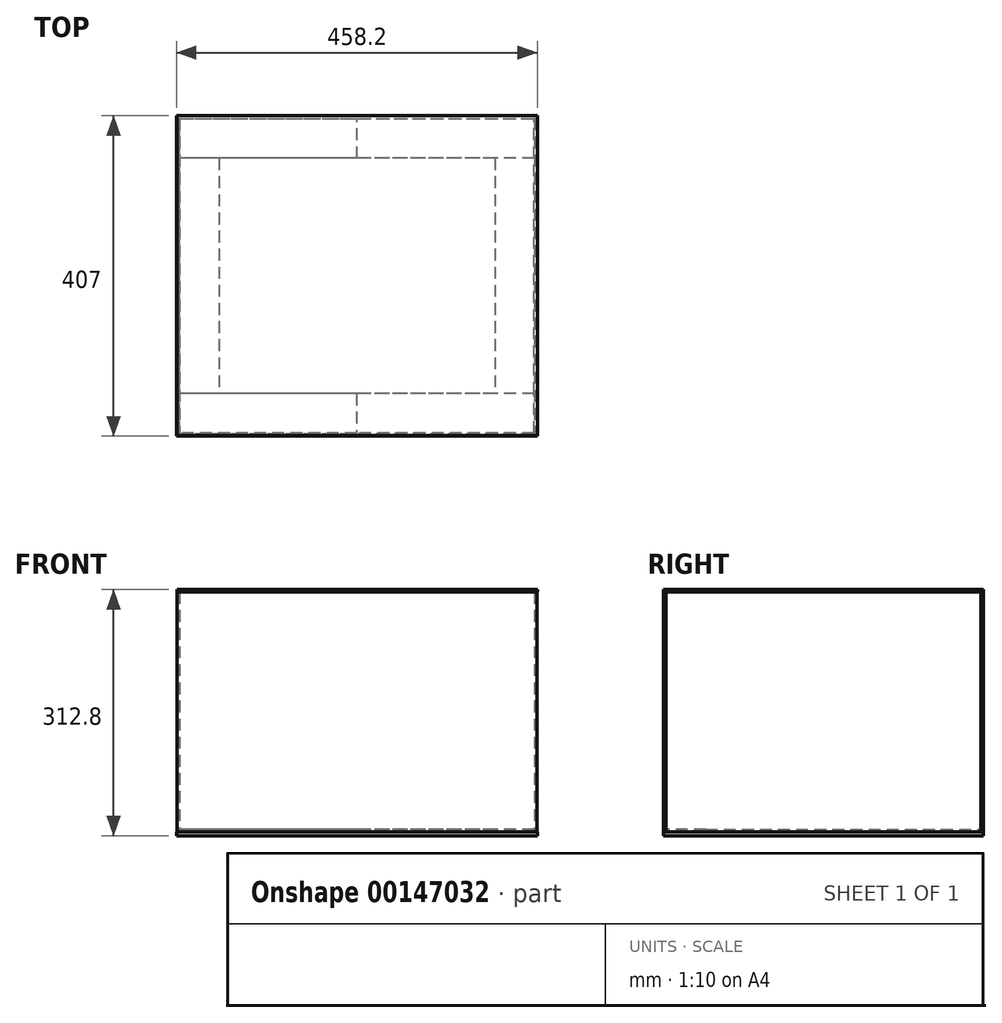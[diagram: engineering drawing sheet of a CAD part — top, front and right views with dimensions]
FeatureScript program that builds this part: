
annotation { "Feature Type Name" : "Feature", "Feature Type Description" : "" }
export const myFeature = defineFeature(function(context is Context, id is Id, definition is map)
    precondition{}
    {
        {
            assignVariable(context, id + "F0", {"name" : "perspex_sheet_width", "anyValue" : 609.6});
        }
        {
            assignVariable(context, id + "F1", {"name" : "perspex_t", "anyValue" : 3});
        }
        {
            assignVariable(context, id + "F2", {"name" : "case_z", "anyValue" : (getVariable(context, 'perspex_sheet_width') / 2) + getVariable(context, 'perspex_t')});
        }
        {
            var Q0;
            Q0=qCreatedBy(makeId("Top.planeOp"),FACE);
            var sketch = newSketch(context, id + "F3", { "sketchPlane" : qUnion([Q0])});
            skLineSegment(sketch, "E0.bottom", {"start": v(-457.7, -406.5) * mm, "end": v(-0.5, -406.5) * mm});
            skLineSegment(sketch, "E0.top", {"start": v(-457.7, -0.5) * mm, "end": v(-0.5, -0.5) * mm});
            skLineSegment(sketch, "E0.left", {"start": v(-457.7, -406.5) * mm, "end": v(-457.7, -0.5) * mm});
            skLineSegment(sketch, "E0.right", {"start": v(-0.5, -406.5) * mm, "end": v(-0.5, -0.5) * mm});
            skLineSegment(sketch, "E1.bottom", {"start": v(0, -407) * mm, "end": v(-458.2, -407) * mm});
            skLineSegment(sketch, "E1.top", {"start": v(0, 0) * mm, "end": v(-458.2, 0) * mm});
            skLineSegment(sketch, "E1.left", {"start": v(0, -407) * mm, "end": v(0, 0) * mm});
            skLineSegment(sketch, "E1.right", {"start": v(-458.2, -407) * mm, "end": v(-458.2, 0) * mm});
            skSolve(sketch);
        }
        {
            assignVariable(context, id + "F4", {"name" : "plywood_t", "anyValue" : 5});
        }
        {
            var Q0;
            Q0=makeQuery(id+"F3.imprint","IMPRINT",FACE,{"disambiguationData":[TD([[makeQuery(id+"F3.imprint","IMPRINT",EDGE,{"derivedFrom":sQuery(id+"F3.wireOp",EDGE,"E0.bottom")}),1.0]])]});
            var Q1;
            Q1=makeQuery(id+"F3.imprint","IMPRINT",FACE,{"disambiguationData":[TD([[makeQuery(id+"F3.imprint","IMPRINT",EDGE,{"derivedFrom":sQuery(id+"F3.wireOp",EDGE,"E0.bottom")}),-1.0]])]});
            extrude(context, id + "F5", {"entities" : qUnion([Q0, Q1]), "depth" : (getVariable(context, 'plywood_t')) * mm});
        }
        {
            var Q0;
            Q0=makeQuery(id+"F5.opExtrude","CAP_FACE",FACE,{"disambiguationData":[OSD([sQuery(id+"F3.wireOp",EDGE,"E1.bottom"),sQuery(id+"F3.wireOp",EDGE,"E1.top"),sQuery(id+"F3.wireOp",EDGE,"E1.left"),sQuery(id+"F3.wireOp",EDGE,"E1.right")])],"isStart":false});
            var sketch = newSketch(context, id + "F6", { "sketchPlane" : qUnion([Q0])});
            skLineSegment(sketch, "E2.bottom", {"start": v(-457.7, -406.5) * mm, "end": v(-0.5, -406.5) * mm});
            skLineSegment(sketch, "E2.top", {"start": v(-457.7, -0.5) * mm, "end": v(-0.5, -0.5) * mm});
            skLineSegment(sketch, "E2.left", {"start": v(-457.7, -406.5) * mm, "end": v(-457.7, -0.5) * mm});
            skLineSegment(sketch, "E2.right", {"start": v(-0.5, -406.5) * mm, "end": v(-0.5, -0.5) * mm});
            skLineSegment(sketch, "E3", {"start": v(-457.7, -403.5) * mm, "end": v(-0.5, -403.5) * mm});
            skLineSegment(sketch, "E4", {"start": v(-457.7, -3.5) * mm, "end": v(-0.5, -3.5) * mm});
            skLineSegment(sketch, "E5", {"start": v(-454.7, -3.5) * mm, "end": v(-454.7, -403.5) * mm});
            skLineSegment(sketch, "E6", {"start": v(-3.5, -3.5) * mm, "end": v(-3.5, -403.5) * mm});
            skLineSegment(sketch, "E7.bottom", {"start": v(-4, -403) * mm, "end": v(-454.2, -403) * mm});
            skLineSegment(sketch, "E7.top", {"start": v(-4, -4) * mm, "end": v(-454.2, -4) * mm});
            skLineSegment(sketch, "E7.left", {"start": v(-4, -403) * mm, "end": v(-4, -4) * mm});
            skLineSegment(sketch, "E7.right", {"start": v(-454.2, -403) * mm, "end": v(-454.2, -4) * mm});
            skLineSegment(sketch, "E8", {"start": v(-4, -54) * mm, "end": v(-454.2, -54) * mm});
            skLineSegment(sketch, "E9", {"start": v(-229.1, -54) * mm, "end": v(-229.1, -4) * mm});
            skLineSegment(sketch, "E10", {"start": v(-4, -353) * mm, "end": v(-454.7, -353) * mm});
            skLineSegment(sketch, "E11", {"start": v(-229.35, -353) * mm, "end": v(-229.35, -403) * mm});
            skLineSegment(sketch, "E12", {"start": v(-54, -54) * mm, "end": v(-54, -353) * mm});
            skLineSegment(sketch, "E13", {"start": v(-404.2, -54) * mm, "end": v(-404.2, -353) * mm});
            skSolve(sketch);
        }
        {
            var Q0;
            {var subQ5=sQuery(id+"F6.wireOp",EDGE,"E5");Q0=makeQuery(id+"F6.imprint","IMPRINT",FACE,{"disambiguationData":[TD([[makeQuery(id+"F6.imprint","IMPRINT",EDGE,{"derivedFrom":subQ5}),-1.0]])]});}
            var Q1;
            {var subQ5=sQuery(id+"F6.wireOp",EDGE,"E6");Q1=makeQuery(id+"F6.imprint","IMPRINT",FACE,{"disambiguationData":[TD([[makeQuery(id+"F6.imprint","IMPRINT",EDGE,{"derivedFrom":subQ5}),1.0]])]});}
            extrude(context, id + "F7", {"entities" : qUnion([Q0, Q1]), "depth" : (getVariable(context, 'case_z') - getVariable(context, 'perspex_t')) * mm});
        }
        {
            var Q0;
            {var subQ1=sQuery(id+"F6.wireOp",EDGE,"E2.bottom");Q0=makeQuery(id+"F6.imprint","IMPRINT",FACE,{"disambiguationData":[TD([[makeQuery(id+"F6.imprint","IMPRINT",EDGE,{"derivedFrom":subQ1}),1.0]])]});}
            var Q1;
            {var subQ1=sQuery(id+"F6.wireOp",EDGE,"E2.top");Q1=makeQuery(id+"F6.imprint","IMPRINT",FACE,{"disambiguationData":[TD([[makeQuery(id+"F6.imprint","IMPRINT",EDGE,{"derivedFrom":subQ1}),-1.0]])]});}
            extrude(context, id + "F8", {"entities" : qUnion([Q0, Q1]), "depth" : (getVariable(context, 'case_z') - getVariable(context, 'perspex_t')) * mm});
        }
        {
            var Q0;
            {var subQ0=sQuery(id+"F6.wireOp",EDGE,"E11");Q0=makeQuery(id+"F6.imprint","IMPRINT",FACE,{"disambiguationData":[TD([[makeQuery(id+"F6.imprint","IMPRINT",EDGE,{"derivedFrom":subQ0}),1.0]])]});}
            var Q1;
            {var subQ0=sQuery(id+"F6.wireOp",EDGE,"E9");Q1=makeQuery(id+"F6.imprint","IMPRINT",FACE,{"disambiguationData":[TD([[makeQuery(id+"F6.imprint","IMPRINT",EDGE,{"derivedFrom":subQ0}),-1.0]])]});}
            var Q2;
            {var subQ5=sQuery(id+"F6.wireOp",EDGE,"E13");Q2=makeQuery(id+"F6.imprint","IMPRINT",FACE,{"disambiguationData":[TD([[makeQuery(id+"F6.imprint","IMPRINT",EDGE,{"derivedFrom":subQ5}),-1.0]])]});}
            extrude(context, id + "F9", {"entities" : qUnion([Q0, Q1, Q2]), "depth" : (getVariable(context, 'perspex_t')) * mm});
        }
        {
            var Q0;
            {var subQ5=sQuery(id+"F6.wireOp",EDGE,"E12");Q0=makeQuery(id+"F6.imprint","IMPRINT",FACE,{"disambiguationData":[TD([[makeQuery(id+"F6.imprint","IMPRINT",EDGE,{"derivedFrom":subQ5}),1.0]])]});}
            var Q1;
            {var subQ4=sQuery(id+"F6.wireOp",EDGE,"E11");Q1=makeQuery(id+"F6.imprint","IMPRINT",FACE,{"disambiguationData":[TD([[makeQuery(id+"F6.imprint","IMPRINT",EDGE,{"derivedFrom":subQ4}),-1.0]])]});}
            var Q2;
            {var subQ0=sQuery(id+"F6.wireOp",EDGE,"E9");Q2=makeQuery(id+"F6.imprint","IMPRINT",FACE,{"disambiguationData":[TD([[makeQuery(id+"F6.imprint","IMPRINT",EDGE,{"derivedFrom":subQ0}),1.0]])]});}
            extrude(context, id + "F10", {"entities" : qUnion([Q0, Q1, Q2]), "depth" : (getVariable(context, 'perspex_t')) * mm});
        }
        {
            var Q0;
            {var subQ2=sQuery(id+"F6.wireOp",EDGE,"E12");Q0=makeQuery(id+"F6.imprint","IMPRINT",FACE,{"disambiguationData":[TD([[makeQuery(id+"F6.imprint","IMPRINT",EDGE,{"derivedFrom":subQ2}),-1.0]])]});}
            extrude(context, id + "F11", {"entities" : qUnion([Q0]), "depth" : (getVariable(context, 'perspex_t')) * mm});
        }
        {
            var Q0;
            Q0=makeQuery(id+"F8.opExtrude","CAP_FACE",FACE,{"disambiguationData":[OSD([sQuery(id+"F6.wireOp",EDGE,"E2.bottom"),sQuery(id+"F6.wireOp",EDGE,"E2.left"),sQuery(id+"F6.wireOp",EDGE,"E2.right"),sQuery(id+"F6.wireOp",EDGE,"E3")])],"isStart":false});
            var sketch = newSketch(context, id + "F12", { "sketchPlane" : qUnion([Q0])});
            skLineSegment(sketch, "E14.bottom", {"start": v(-457.7, -406.5) * mm, "end": v(0, -406.5) * mm});
            skLineSegment(sketch, "E14.top", {"start": v(-457.7, 0) * mm, "end": v(0, 0) * mm});
            skLineSegment(sketch, "E14.left", {"start": v(-457.7, -406.5) * mm, "end": v(-457.7, 0) * mm});
            skLineSegment(sketch, "E14.right", {"start": v(0, -406.5) * mm, "end": v(0, 0) * mm});
            skSolve(sketch);
        }
        {
            var Q0;
            {var subQ4=sQuery(id+"F12.wireOp",EDGE,"E14.top");Q0=makeQuery(id+"F12.imprint","IMPRINT",FACE,{"disambiguationData":[TD([[makeQuery(id+"F12.imprint","IMPRINT",EDGE,{"derivedFrom":subQ4}),-1.0]])]});}
            var Q1;
            {var subQ4=sQuery(id+"F6.wireOp",EDGE,"E3");var subQ6=makeQuery(id+"F8.opExtrude","CAP_EDGE",EDGE,{"disambiguationData":[OSD([subQ4])],"isStart":false});Q1=makeQuery(id+"F12.imprint","IMPRINT",FACE,{"disambiguationData":[TD([[makeQuery(id+"F12.imprint","IMPRINT",EDGE,{"derivedFrom":subQ6}),-1.0]])]});}
            extrude(context, id + "F13", {"entities" : qUnion([Q0, Q1]), "depth" : (getVariable(context, 'perspex_t')) * mm});
        }
    });
